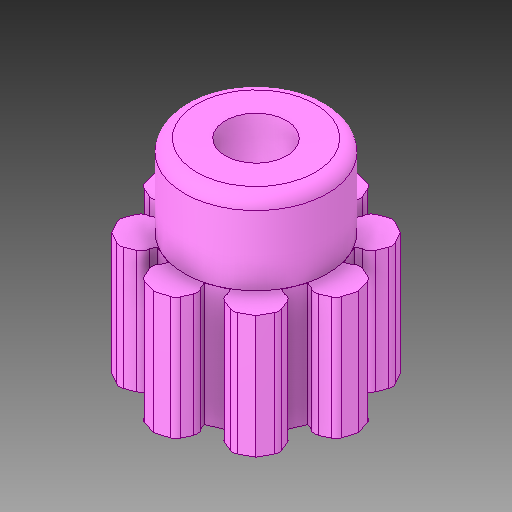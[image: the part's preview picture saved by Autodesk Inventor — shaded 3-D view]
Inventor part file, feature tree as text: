
AUTODESK INVENTOR PART (.ipt)
format: ipt  version: 2019.1 (Build 231200000, 200)  size: 246,272 bytes
history: mixed  units: in
note: dims shown in document units (in); Inventor stores cm internally (conversion verified against a paired STEP export)
features: fillet x1, imported_body x1
ambient origin geometry x8: Origin, YZ Plane, XZ Plane, XY Plane, X Axis, Y Axis, Z Axis, Center Point
bodies: Solid1 (imported_parasolid)
feature tree (2):
  fillet  "Fillet1"  [1 undecoded]
  imported_body  NMx_Import_Brep_tag  [imported B-rep: ~119 faces, bbox_mm=[5.0, 5.0, 5.0]]
note: 1 required parameter value undecoded (feature->parameter linkage not recoverable at this tier; creation-order binding heuristic only, values carry confidence <= 0.55)
